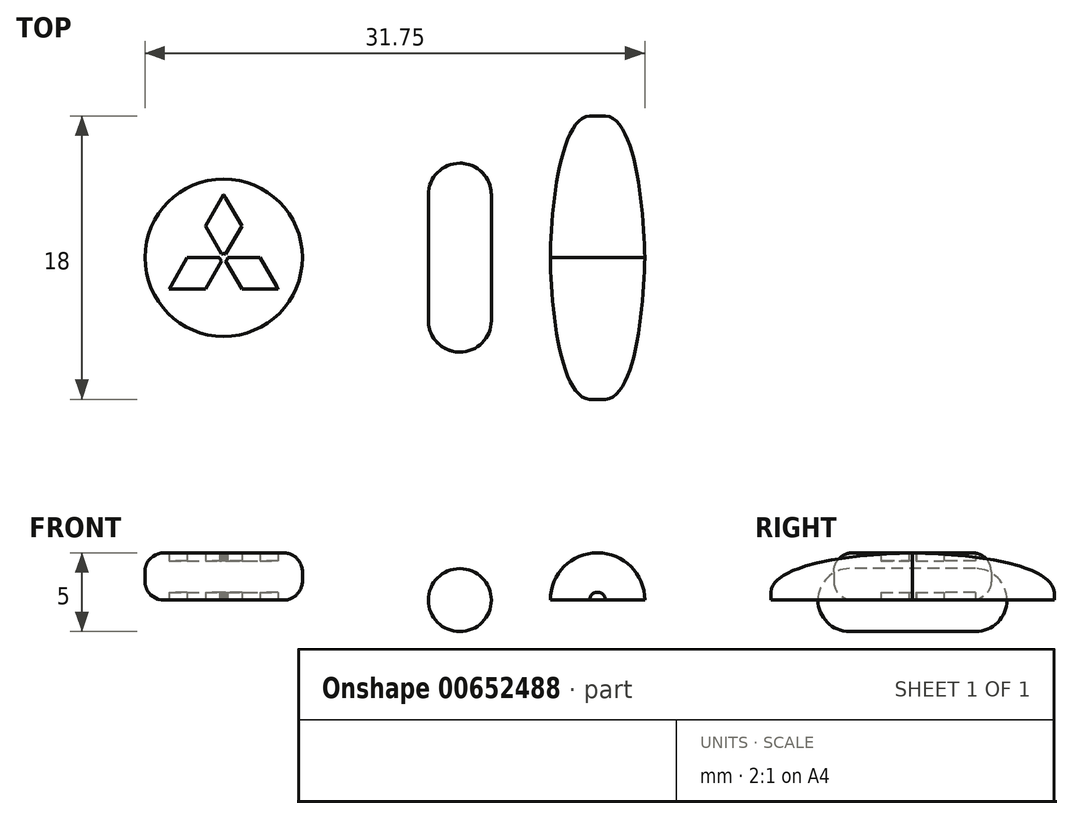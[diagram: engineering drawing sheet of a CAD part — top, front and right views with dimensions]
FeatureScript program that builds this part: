
annotation { "Feature Type Name" : "Feature", "Feature Type Description" : "" }
export const myFeature = defineFeature(function(context is Context, id is Id, definition is map)
    precondition{}
    {
        {
            var Q0;
            Q0=qCreatedBy(makeId("Top.planeOp"),FACE);
            var sketch = newSketch(context, id + "F0", { "sketchPlane" : qUnion([Q0])});
            skLineSegment(sketch, "E0", {"start": v(0, 0) * mm, "end": v(0, 6) * mm});
            skArc(sketch, "E1", {"start": v(2, 4) * mm, "mid": v(1.41, 5.41) * mm, "end": v(0, 6) * mm});
            skPoint(sketch, "E2", {"position": v(2, 4) * mm});
            skArc(sketch, "E3.MirrorCS", {"start": v(2, -4) * mm, "mid": v(1.41, -5.41) * mm, "end": v(0, -6) * mm});
            skPoint(sketch, "E4.MirrorP", {"position": v(2, -4) * mm});
            skLineSegment(sketch, "E5.MirrorCS", {"start": v(0, 0) * mm, "end": v(0, -6) * mm});
            skLineSegment(sketch, "E6", {"start": v(2, -4) * mm, "end": v(2, 4) * mm});
            skSolve(sketch);
        }
        {
            var Q0;
            Q0=makeQuery(id+"F0.imprint","IMPRINT",FACE,{"disambiguationData":[TD([[makeQuery(id+"F0.imprint","IMPRINT",EDGE,{"derivedFrom":sQuery(id+"F0.wireOp",EDGE,"E0")}),-1.0]])]});
            var Q1;
            Q1=sQuery(id+"F0.wireOp",EDGE,"E0");
            revolve(context, id + "F1", {"entities" : qUnion([Q0]), "axis" : qUnion([Q1]), "revolveType" : RevolveType.FULL});
        }
        {
            var Q0;
            Q0=qCreatedBy(makeId("Top.planeOp"),FACE);
            var sketch = newSketch(context, id + "F2", { "sketchPlane" : qUnion([Q0])});
            skCircle(sketch, "E7", {"center": v(-15, 0) * mm, "radius": 5 * mm});
            skLineSegment(sketch, "E8", {"start": v(-15, 4) * mm, "end": v(-16.15, 2) * mm});
            skLineSegment(sketch, "E9", {"start": v(-18.46, -2) * mm, "end": v(-16.15, -2) * mm});
            skLineSegment(sketch, "E10", {"start": v(-11.54, -2) * mm, "end": v(-12.7, 0) * mm});
            skLineSegment(sketch, "E11", {"start": v(-16.15, 2) * mm, "end": v(-15.12, 0.22) * mm});
            skLineSegment(sketch, "E12", {"start": v(-14.88, 0.22) * mm, "end": v(-13.85, 2) * mm});
            skLineSegment(sketch, "E13", {"start": v(-14.75, 0) * mm, "end": v(-12.7, 0) * mm});
            skLineSegment(sketch, "E14", {"start": v(-13.85, -2) * mm, "end": v(-14.88, -0.22) * mm});
            skLineSegment(sketch, "E15", {"start": v(-17.3, 0) * mm, "end": v(-15.25, 0) * mm});
            skLineSegment(sketch, "E16", {"start": v(-16.15, -2) * mm, "end": v(-15.12, -0.22) * mm});
            skLineSegment(sketch, "E17.trimOffspring", {"start": v(-13.85, 2) * mm, "end": v(-15, 4) * mm});
            skLineSegment(sketch, "E18.trimOffspring", {"start": v(-17.3, 0) * mm, "end": v(-18.46, -2) * mm});
            skLineSegment(sketch, "E19.trimOffspring", {"start": v(-13.85, -2) * mm, "end": v(-11.54, -2) * mm});
            skCircle(sketch, "E20", {"center": v(-15, 0) * mm, "radius": 0.25 * mm});
            skSolve(sketch);
        }
        {
            var Q0;
            Q0=makeQuery(id+"F2.imprint","IMPRINT",FACE,{"disambiguationData":[TD([[makeQuery(id+"F2.imprint","IMPRINT",EDGE,{"derivedFrom":sQuery(id+"F2.wireOp",EDGE,"E7")}),1.0]])]});
            var Q1;
            {var subQ0=sQuery(id+"F2.wireOp",EDGE,"E20");var subQ4=makeQuery(id+"F2.imprint","INTERSECT",VERTEX,{"derivedFrom":[sQuery(id+"F2.wireOp",EDGE,"E12"),subQ0]});Q1=makeQuery(id+"F2.imprint","IMPRINT",FACE,{"disambiguationData":[TD([[makeQuery(id+"F2.imprint","IMPRINT",EDGE,{"disambiguationData":[TD([[subQ4,1.0]])],"derivedFrom":subQ0}),1.0]])]});}
            extrude(context, id + "F3", {"entities" : qUnion([Q0, Q1]), "depth" : 3 * mm, "offsetDistance" : 25 * mm});
        }
        {
            var Q0;
            Q0=makeQuery(id+"F2.imprint","IMPRINT",FACE,{"disambiguationData":[TD([[makeQuery(id+"F2.imprint","IMPRINT",EDGE,{"derivedFrom":sQuery(id+"F2.wireOp",EDGE,"E9")}),1.0]])]});
            var Q1;
            Q1=makeQuery(id+"F2.imprint","IMPRINT",FACE,{"disambiguationData":[TD([[makeQuery(id+"F2.imprint","IMPRINT",EDGE,{"derivedFrom":sQuery(id+"F2.wireOp",EDGE,"E10")}),1.0]])]});
            var Q2;
            Q2=makeQuery(id+"F2.imprint","IMPRINT",FACE,{"disambiguationData":[TD([[makeQuery(id+"F2.imprint","IMPRINT",EDGE,{"derivedFrom":sQuery(id+"F2.wireOp",EDGE,"E8")}),1.0]])]});
            var Q3;
            Q3=makeQuery(id+"F3.opExtrude","CAP_FACE",FACE,{"disambiguationData":[OSD([sQuery(id+"F2.wireOp",EDGE,"E7"),sQuery(id+"F2.wireOp",EDGE,"E8"),sQuery(id+"F2.wireOp",EDGE,"E9"),sQuery(id+"F2.wireOp",EDGE,"E10"),sQuery(id+"F2.wireOp",EDGE,"E11"),sQuery(id+"F2.wireOp",EDGE,"E12"),sQuery(id+"F2.wireOp",EDGE,"E13"),sQuery(id+"F2.wireOp",EDGE,"E14"),sQuery(id+"F2.wireOp",EDGE,"E15"),sQuery(id+"F2.wireOp",EDGE,"E16"),sQuery(id+"F2.wireOp",EDGE,"E17.trimOffspring"),sQuery(id+"F2.wireOp",EDGE,"E18.trimOffspring"),sQuery(id+"F2.wireOp",EDGE,"E19.trimOffspring"),sQuery(id+"F2.wireOp",EDGE,"E20")])],"isStart":false});
            extrude(context, id + "F4", {"entities" : qUnion([Q0, Q1, Q2]), "operationType" : NewBodyOperationType.ADD, "endBound" : BoundingType.UP_TO_SURFACE, "depth" : 3.5 * mm, "endBoundEntityFace" : qUnion([Q3]), "hasOffset" : true, "offsetDistance" : 0.5 * mm, "hasSecondDirection" : true, "secondDirectionOppositeDirection" : false, "secondDirectionDepth" : 0.5 * mm});
        }
        {
            var Q0;
            Q0=makeQuery(id+"F3.opExtrude","SWEPT_FACE",FACE,{"disambiguationData":[OSD([sQuery(id+"F2.wireOp",EDGE,"E7")])]});
            fillet(context, id + "F5", {"entities" : qUnion([Q0]), "radius" : 1.2 * mm, "tangentPropagation" : true, "allowEdgeOverflow" : false});
        }
        {
            var Q0;
            Q0=qCreatedBy(makeId("Top.planeOp"),FACE);
            var sketch = newSketch(context, id + "F6", { "sketchPlane" : qUnion([Q0])});
            skLineSegment(sketch, "E21", {"start": v(8.75, 0) * mm, "end": v(8.75, 9) * mm});
            skLineSegment(sketch, "E22", {"start": v(8.75, 9) * mm, "end": v(9.25, 9) * mm});
            skFitSpline(sketch, "E23", {"points": [v(9.25, 9) * mm, v(11.75, 0) * mm], "startDerivative": vector(5.82, -0.46) * mm, "endDerivative": vector(0.15, -8.91) * mm});
            skFitSpline(sketch, "E24.MirrorCS", {"points": [v(9.25, -9) * mm, v(11.75, 0) * mm], "startDerivative": vector(5.82, 0.46) * mm, "endDerivative": vector(0.15, 8.91) * mm});
            skLineSegment(sketch, "E25.MirrorCS", {"start": v(8.75, -9) * mm, "end": v(9.25, -9) * mm});
            skLineSegment(sketch, "E26.MirrorCS", {"start": v(8.75, 0) * mm, "end": v(8.75, -9) * mm});
            skSolve(sketch);
        }
        {
            var Q0;
            Q0=makeQuery(id+"F6.imprint","IMPRINT",FACE,{"disambiguationData":[TD([[makeQuery(id+"F6.imprint","IMPRINT",EDGE,{"derivedFrom":sQuery(id+"F6.wireOp",EDGE,"E21")}),-1.0]])]});
            var Q1;
            Q1=sQuery(id+"F6.wireOp",EDGE,"E21");
            revolve(context, id + "F7", {"surfaceOperationType" : NewSurfaceOperationType.NEW, "entities" : qUnion([Q0]), "axis" : qUnion([Q1]), "revolveType" : RevolveType.ONE_DIRECTION, "oppositeDirection" : true, "angle" : 180 * degree});
        }
    });
